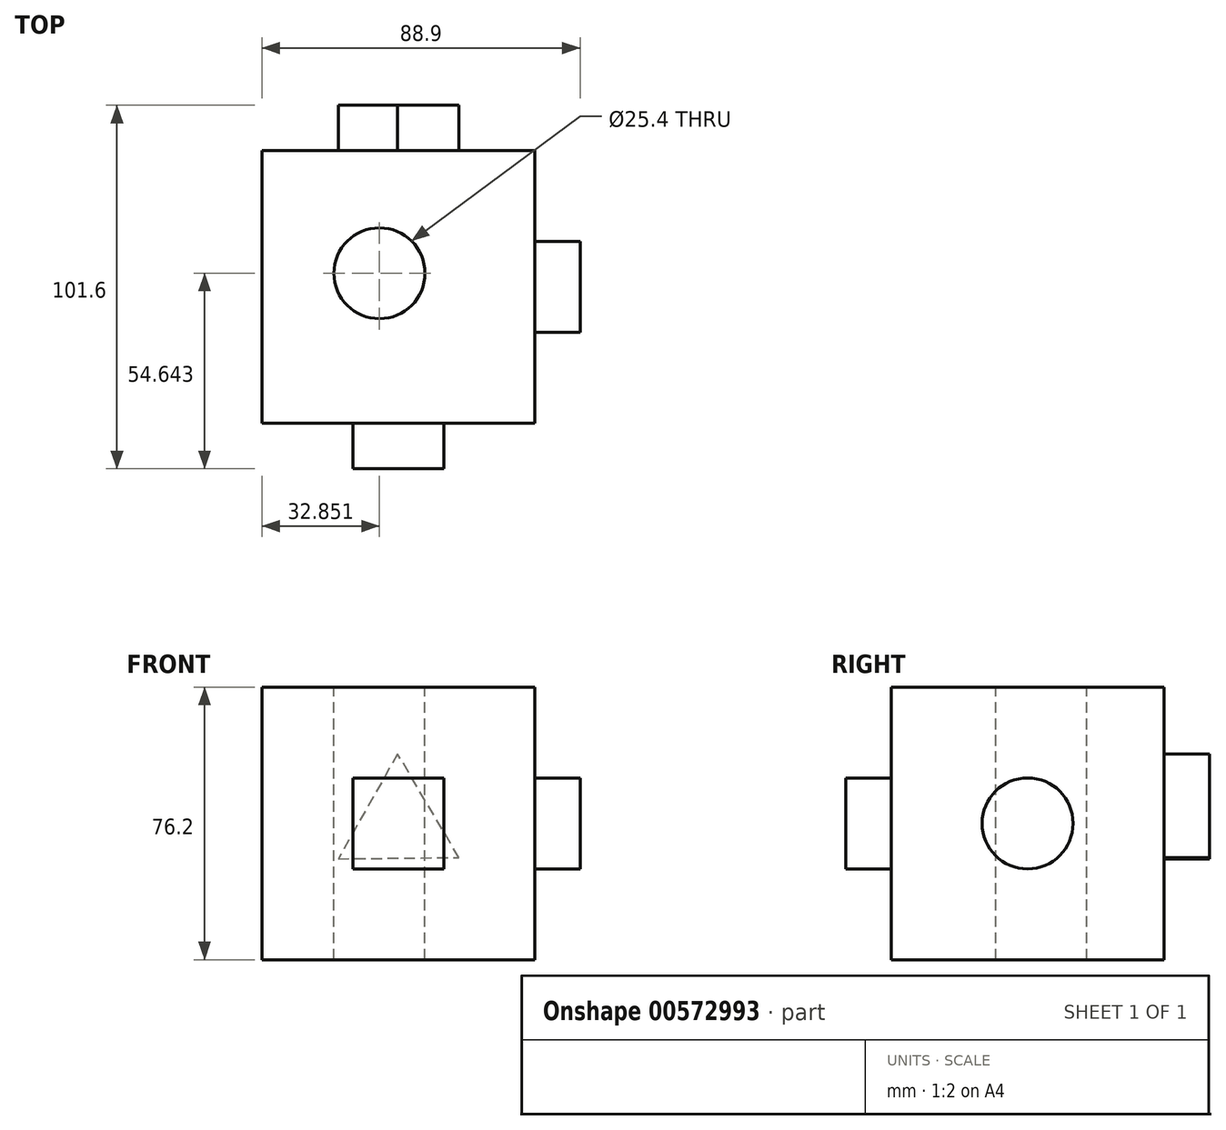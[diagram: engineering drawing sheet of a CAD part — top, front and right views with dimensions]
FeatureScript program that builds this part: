
annotation { "Feature Type Name" : "Feature", "Feature Type Description" : "" }
export const myFeature = defineFeature(function(context is Context, id is Id, definition is map)
    precondition{}
    {
        {
            var Q0;
            Q0=qCreatedBy(makeId("Front.planeOp"),FACE);
            var sketch = newSketch(context, id + "F0", { "sketchPlane" : qUnion([Q0])});
            skLineSegment(sketch, "E0.bottom", {"start": v(-87.44, 29.7) * mm, "end": v(-11.24, 29.7) * mm});
            skLineSegment(sketch, "E0.top", {"start": v(-87.44, 105.9) * mm, "end": v(-11.24, 105.9) * mm});
            skLineSegment(sketch, "E0.left", {"start": v(-87.44, 29.7) * mm, "end": v(-87.44, 105.9) * mm});
            skLineSegment(sketch, "E0.right", {"start": v(-11.24, 29.7) * mm, "end": v(-11.24, 105.9) * mm});
            skSolve(sketch);
        }
        {
            var Q0;
            Q0=makeQuery(id+"F0.imprint","IMPRINT",FACE,{"disambiguationData":[TD([[makeQuery(id+"F0.imprint","IMPRINT",EDGE,{"derivedFrom":sQuery(id+"F0.wireOp",EDGE,"E0.bottom")}),1.0]])]});
            extrude(context, id + "F1", {"entities" : qUnion([Q0]), "depth" : 76.2 * mm, "offsetDistance" : 25.4 * mm});
        }
        {
            var Q0;
            Q0=makeQuery(id+"F1.opExtrude","SWEPT_FACE",FACE,{"disambiguationData":[OSD([sQuery(id+"F0.wireOp",EDGE,"E0.right")])]});
            var sketch = newSketch(context, id + "F2", { "sketchPlane" : qUnion([Q0])});
            skCircle(sketch, "E1", {"center": v(-38.1, 67.8) * mm, "radius": 12.7 * mm});
            skSolve(sketch);
        }
        {
            var Q0;
            Q0=makeQuery(id+"F2.imprint","IMPRINT",FACE,{"disambiguationData":[TD([[makeQuery(id+"F2.imprint","IMPRINT",EDGE,{"derivedFrom":sQuery(id+"F2.wireOp",EDGE,"E1")}),1.0]])]});
            extrude(context, id + "F3", {"entities" : qUnion([Q0]), "operationType" : NewBodyOperationType.ADD, "depth" : 12.7 * mm, "offsetDistance" : 25.4 * mm});
        }
        {
            var Q0;
            Q0=makeQuery(id+"F1.opExtrude","CAP_FACE",FACE,{"disambiguationData":[OSD([sQuery(id+"F0.wireOp",EDGE,"E0.bottom"),sQuery(id+"F0.wireOp",EDGE,"E0.top"),sQuery(id+"F0.wireOp",EDGE,"E0.left"),sQuery(id+"F0.wireOp",EDGE,"E0.right")])],"isStart":false});
            var sketch = newSketch(context, id + "F4", { "sketchPlane" : qUnion([Q0])});
            skLineSegment(sketch, "E2.bottom", {"start": v(-62.04, 55.1) * mm, "end": v(-36.64, 55.1) * mm});
            skLineSegment(sketch, "E2.top", {"start": v(-62.04, 80.5) * mm, "end": v(-36.64, 80.5) * mm});
            skLineSegment(sketch, "E2.left", {"start": v(-62.04, 55.1) * mm, "end": v(-62.04, 80.5) * mm});
            skLineSegment(sketch, "E2.right", {"start": v(-36.64, 55.1) * mm, "end": v(-36.64, 80.5) * mm});
            skSolve(sketch);
        }
        {
            var Q0;
            Q0=makeQuery(id+"F4.imprint","IMPRINT",FACE,{"disambiguationData":[TD([[makeQuery(id+"F4.imprint","IMPRINT",EDGE,{"derivedFrom":sQuery(id+"F4.wireOp",EDGE,"E2.bottom")}),1.0]])]});
            extrude(context, id + "F5", {"entities" : qUnion([Q0]), "operationType" : NewBodyOperationType.ADD, "depth" : 12.7 * mm, "offsetDistance" : 25.4 * mm});
        }
        {
            var Q0;
            Q0=makeQuery(id+"F1.opExtrude","SWEPT_FACE",FACE,{"disambiguationData":[OSD([sQuery(id+"F0.wireOp",EDGE,"E0.top")])]});
            var sketch = newSketch(context, id + "F6", { "sketchPlane" : qUnion([Q0])});
            skPoint(sketch, "E3", {"position": v(-54.59, -34.26) * mm});
            skSolve(sketch);
        }
        {
            var Q0;
            Q0=sQuery(id+"F6.wireOp",VERTEX,"E3");
            var Q1;
            Q1=makeQuery(id+"F1.opExtrude","SWEPT_BODY",BODY,{"disambiguationData":[OSD([sQuery(id+"F0.wireOp",EDGE,"E0.bottom"),sQuery(id+"F0.wireOp",EDGE,"E0.top"),sQuery(id+"F0.wireOp",EDGE,"E0.left"),sQuery(id+"F0.wireOp",EDGE,"E0.right")])]});
            hole(context, id + "F7", {"style" : HoleStyle.SIMPLE, "endStyle" : HoleEndStyle.THROUGH, "holeDiameter" : 25.4 * mm, "isTappedThrough" : true, "tappedDepth" : 12.7 * mm, "tapClearance" : 3, "locations" : qUnion([Q0]), "scope" : qUnion([Q1])});
        }
        {
            var Q0;
            Q0=makeQuery(id+"F1.opExtrude","CAP_FACE",FACE,{"disambiguationData":[OSD([sQuery(id+"F0.wireOp",EDGE,"E0.bottom"),sQuery(id+"F0.wireOp",EDGE,"E0.top"),sQuery(id+"F0.wireOp",EDGE,"E0.left"),sQuery(id+"F0.wireOp",EDGE,"E0.right")])],"isStart":true});
            var sketch = newSketch(context, id + "F8", { "sketchPlane" : qUnion([Q0])});
            skCircle(sketch, "E4.cCircle", {"center": v(49.34, 67.8) * mm, "radius": 9.72 * mm, "construction": true});
            skLineSegment(sketch, "E4.0", {"start": v(49.54, 87.25) * mm, "end": v(66.09, 57.92) * mm});
            skLineSegment(sketch, "E4.1", {"start": v(66.09, 57.92) * mm, "end": v(32.4, 58.25) * mm});
            skLineSegment(sketch, "E4.2", {"start": v(32.4, 58.25) * mm, "end": v(49.54, 87.25) * mm});
            skPoint(sketch, "E4.0.midPoint", {"position": v(57.81, 72.58) * mm});
            skSolve(sketch);
        }
        {
            var Q0;
            Q0=makeQuery(id+"F8.imprint","IMPRINT",FACE,{"disambiguationData":[TD([[makeQuery(id+"F8.imprint","IMPRINT",EDGE,{"derivedFrom":sQuery(id+"F8.wireOp",EDGE,"E4.0")}),-1.0]])]});
            extrude(context, id + "F9", {"entities" : qUnion([Q0]), "operationType" : NewBodyOperationType.ADD, "depth" : 12.7 * mm, "offsetDistance" : 25.4 * mm});
        }
    });
